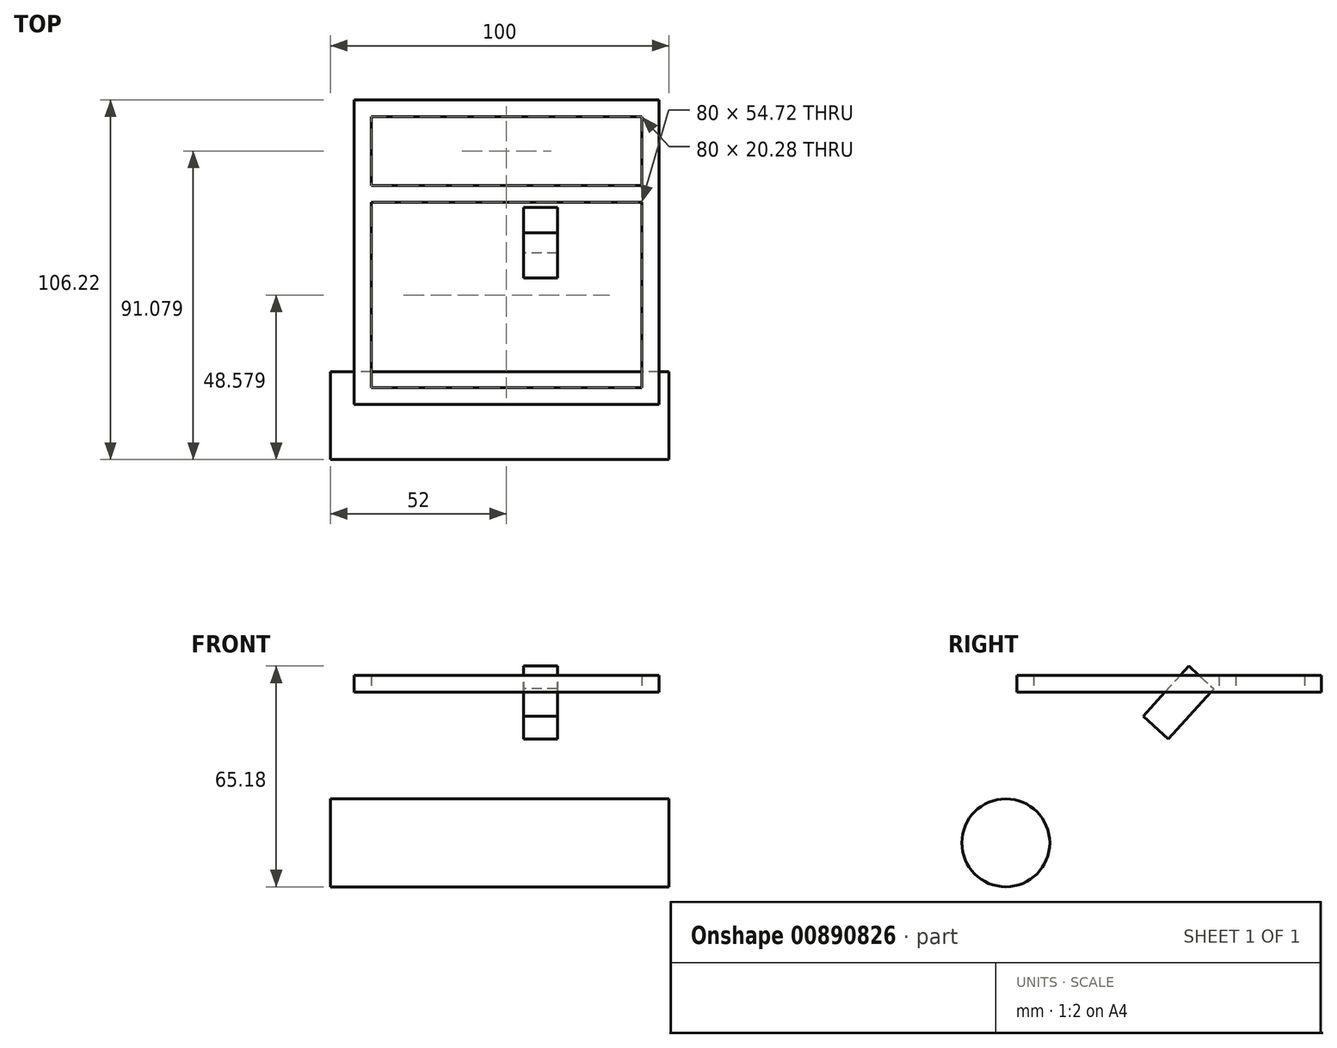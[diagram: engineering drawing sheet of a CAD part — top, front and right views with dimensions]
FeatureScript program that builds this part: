
annotation { "Feature Type Name" : "Feature", "Feature Type Description" : "" }
export const myFeature = defineFeature(function(context is Context, id is Id, definition is map)
    precondition{}
    {
        {
            var Q0;
            Q0=qCreatedBy(makeId("Top.planeOp"),FACE);
            var sketch = newSketch(context, id + "F0", { "sketchPlane" : qUnion([Q0])});
            skLineSegment(sketch, "E0.bottom", {"start": v(-40, 40) * mm, "end": v(40, 40) * mm});
            skLineSegment(sketch, "E0.top", {"start": v(-40, -40) * mm, "end": v(40, -40) * mm});
            skLineSegment(sketch, "E0.left", {"start": v(-40, 40) * mm, "end": v(-40, -40) * mm});
            skLineSegment(sketch, "E0.right", {"start": v(40, 40) * mm, "end": v(40, -40) * mm});
            skLineSegment(sketch, "E1.bottom", {"start": v(-45, 45) * mm, "end": v(45, 45) * mm});
            skLineSegment(sketch, "E1.top", {"start": v(-45, -45) * mm, "end": v(45, -45) * mm});
            skLineSegment(sketch, "E1.left", {"start": v(-45, 45) * mm, "end": v(-45, -45) * mm});
            skLineSegment(sketch, "E1.right", {"start": v(45, 45) * mm, "end": v(45, -45) * mm});
            skLineSegment(sketch, "E2", {"start": v(-40, 19.72) * mm, "end": v(40, 19.72) * mm});
            skLineSegment(sketch, "E3", {"start": v(-40, 14.72) * mm, "end": v(40, 14.72) * mm});
            skSolve(sketch);
        }
        {
            var Q0;
            Q0 = qSketchRegion(id + "F0", true);
            var Q1;
            {var subQ0=sQuery(id+"F0.wireOp",EDGE,"E2");Q1=makeQuery(id+"F0.imprint","IMPRINT",FACE,{"disambiguationData":[TD([[makeQuery(id+"F0.imprint","IMPRINT",EDGE,{"derivedFrom":subQ0}),-1.0]])]});}
            extrude(context, id + "F1", {"entities" : qUnion([Q0, Q1]), "depth" : 5 * mm, "offsetDistance" : 25 * mm});
        }
        {
            var Q0;
            Q0=makeQuery(id+"F1.opExtrude","SWEPT_FACE",FACE,{"disambiguationData":[OSD([sQuery(id+"F0.wireOp",EDGE,"E1.right")])]});
            var sketch = newSketch(context, id + "F2", { "sketchPlane" : qUnion([Q0])});
            skLineSegment(sketch, "E4", {"start": v(6.18, -8.98) * mm, "end": v(-7.26, -23.79) * mm});
            skLineSegment(sketch, "E5", {"start": v(-7.26, -23.79) * mm, "end": v(-14.67, -17.07) * mm});
            skLineSegment(sketch, "E6", {"start": v(-14.67, -17.07) * mm, "end": v(-1.23, -2.26) * mm});
            skLineSegment(sketch, "E7", {"start": v(-1.23, -2.26) * mm, "end": v(6.18, -8.98) * mm});
            skCircle(sketch, "E8", {"center": v(-48.24, -44.45) * mm, "radius": 12.99 * mm});
            skSolve(sketch);
        }
        {
            var Q0;
            Q0 = qSketchRegion(id + "F2", true);
            extrude(context, id + "F3", {"entities" : qUnion([Q0]), "depth" : 10 * mm, "offsetDistance" : 25 * mm});
        }
        {
            var Q0;
            Q0=makeQuery(id+"F3.opExtrude","SWEPT_BODY",BODY,{"disambiguationData":[OSD([sQuery(id+"F2.wireOp",EDGE,"E4"),sQuery(id+"F2.wireOp",EDGE,"E5"),sQuery(id+"F2.wireOp",EDGE,"E6"),sQuery(id+"F2.wireOp",EDGE,"E7")])]});
            transform(context, id + "F4", {"entities" : qUnion([Q0]), "transformType" : TransformType.TRANSLATION_3D, "dx" : -40 * mm, "dy" : 7 * mm, "dz" : 10 * mm, "makeCopy" : false});
        }
        {
            var Q0;
            Q0=makeQuery(id+"F3.opExtrude","CAP_FACE",FACE,{"disambiguationData":[OSD([sQuery(id+"F2.wireOp",EDGE,"E8")])],"isStart":false});
            extrude(context, id + "F5", {"entities" : qUnion([Q0]), "operationType" : NewBodyOperationType.ADD, "depth" : -100 * mm, "offsetDistance" : 25 * mm});
        }
        {
            var Q0;
            Q0=makeQuery(id+"F3.opExtrude","SWEPT_BODY",BODY,{"disambiguationData":[OSD([sQuery(id+"F2.wireOp",EDGE,"E8")])]});
            transform(context, id + "F6", {"entities" : qUnion([Q0]), "transformType" : TransformType.TRANSLATION_3D, "dx" : -7 * mm, "dy" : 0 * mm, "dz" : 0 * mm, "makeCopy" : false});
        }
    });
